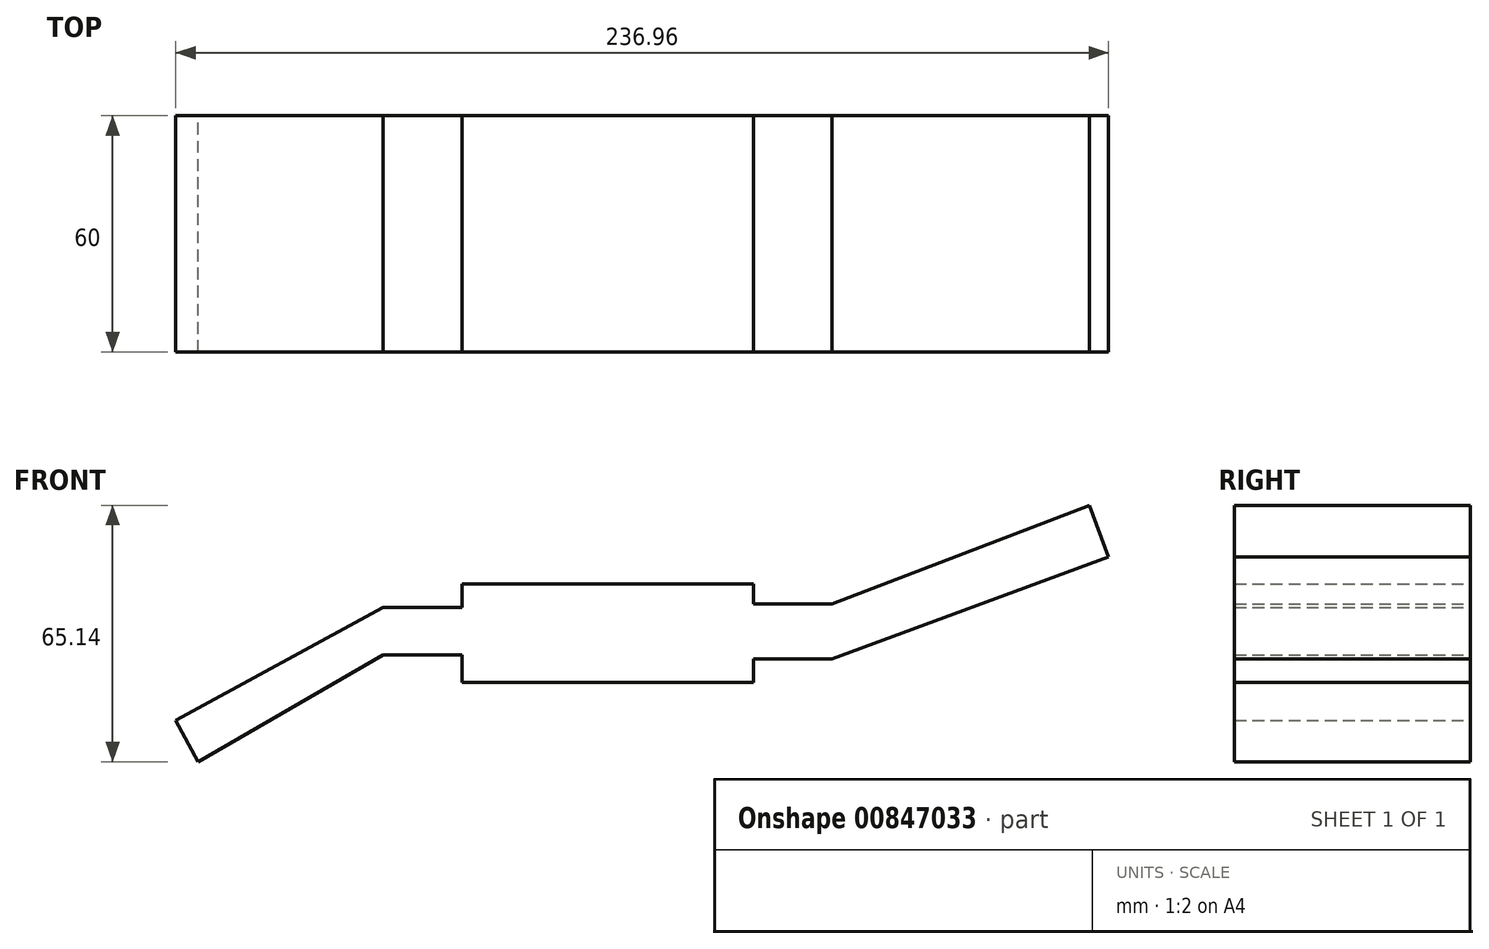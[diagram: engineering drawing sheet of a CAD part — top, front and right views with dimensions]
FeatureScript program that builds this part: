
annotation { "Feature Type Name" : "Feature", "Feature Type Description" : "" }
export const myFeature = defineFeature(function(context is Context, id is Id, definition is map)
    precondition{}
    {
        {
            var Q0;
            Q0=qCreatedBy(makeId("Front.planeOp"),FACE);
            var sketch = newSketch(context, id + "F0", { "sketchPlane" : qUnion([Q0])});
            skLineSegment(sketch, "E0.bottom", {"start": v(37, 12.5) * mm, "end": v(-37, 12.5) * mm});
            skLineSegment(sketch, "E0.top", {"start": v(37, -12.5) * mm, "end": v(-37, -12.5) * mm});
            skLineSegment(sketch, "E0.left", {"start": v(37, 12.5) * mm, "end": v(37, -12.5) * mm});
            skLineSegment(sketch, "E0.right", {"start": v(-37, 12.5) * mm, "end": v(-37, -12.5) * mm});
            skPoint(sketch, "E0.middle", {"position": v(0, 0) * mm});
            skLineSegment(sketch, "E1", {"start": v(37, -6.5) * mm, "end": v(57, -6.5) * mm});
            skLineSegment(sketch, "E2", {"start": v(37, 7.5) * mm, "end": v(57, 7.5) * mm});
            skLineSegment(sketch, "E3", {"start": v(57, -6.5) * mm, "end": v(127.22, 19.35) * mm});
            skLineSegment(sketch, "E4", {"start": v(127.22, 19.35) * mm, "end": v(122.39, 32.49) * mm});
            skLineSegment(sketch, "E5", {"start": v(122.39, 32.49) * mm, "end": v(57, 7.5) * mm});
            skLineSegment(sketch, "E6", {"start": v(-37, -5.5) * mm, "end": v(-57, -5.5) * mm});
            skLineSegment(sketch, "E7", {"start": v(-109.74, -22.1) * mm, "end": v(-57, 6.5) * mm});
            skLineSegment(sketch, "E8", {"start": v(-57, 6.5) * mm, "end": v(-37, 6.5) * mm});
            skLineSegment(sketch, "E9", {"start": v(-109.74, -22.1) * mm, "end": v(-104.02, -32.65) * mm});
            skLineSegment(sketch, "E10", {"start": v(-104.02, -32.65) * mm, "end": v(-57, -5.5) * mm});
            skSolve(sketch);
        }
        {
            var Q0;
            Q0 = qSketchRegion(id + "F0", true);
            extrude(context, id + "F1", {"entities" : qUnion([Q0]), "endBound" : BoundingType.SYMMETRIC, "depth" : 60 * mm, "offsetDistance" : 25 * mm});
        }
    });
